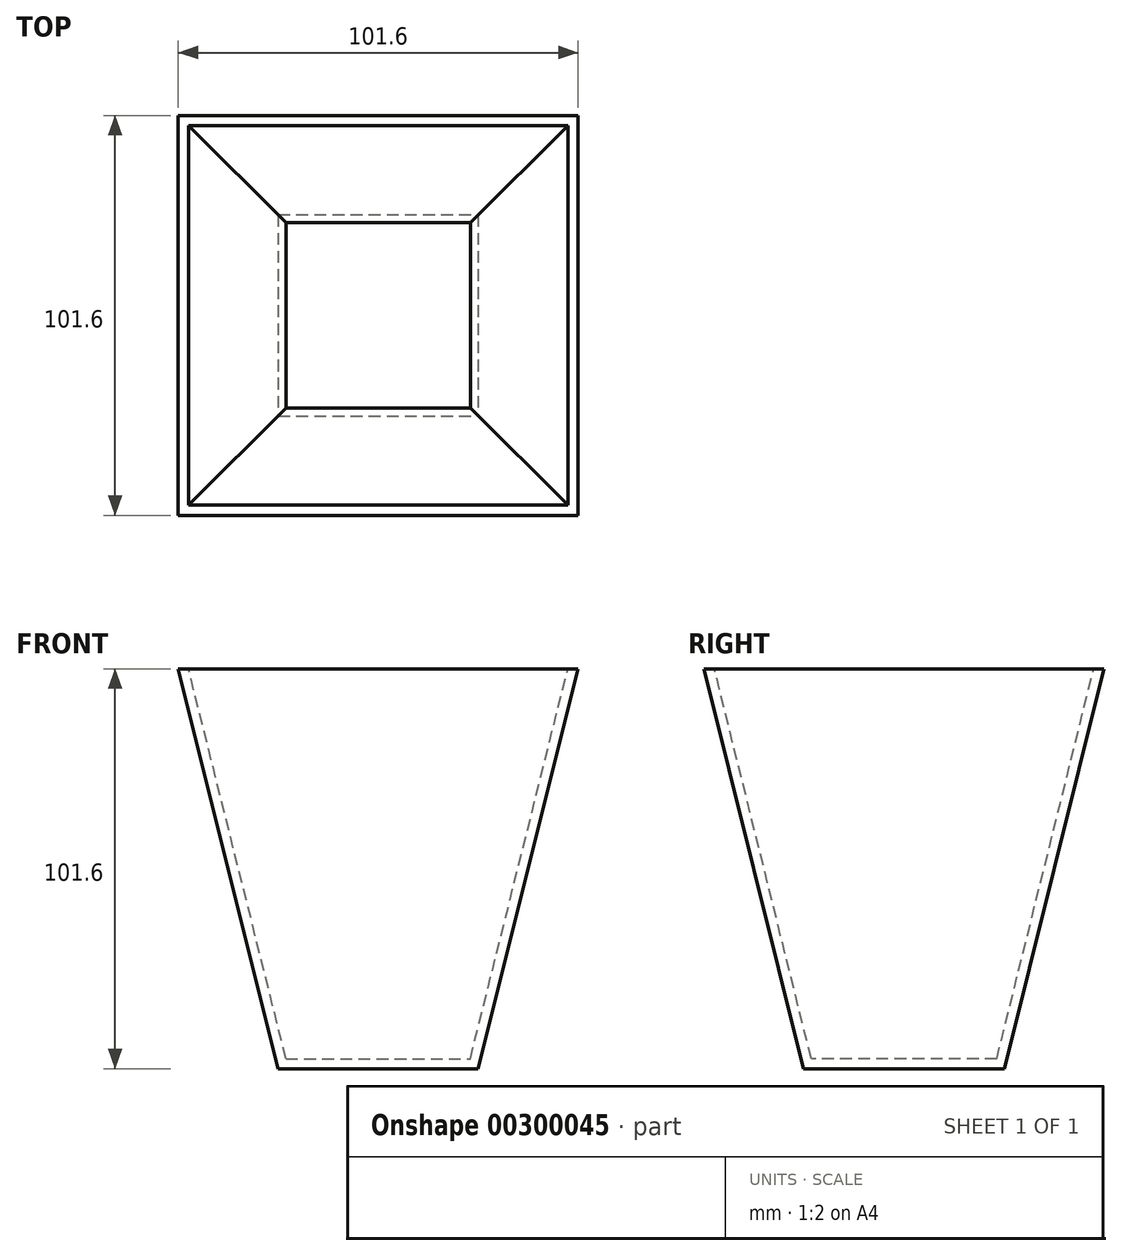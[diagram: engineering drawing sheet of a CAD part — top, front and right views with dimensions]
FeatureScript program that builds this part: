
annotation { "Feature Type Name" : "Feature", "Feature Type Description" : "" }
export const myFeature = defineFeature(function(context is Context, id is Id, definition is map)
    precondition{}
    {
        {
            var Q0;
            Q0=qCreatedBy(makeId("Front.planeOp"),FACE);
            var sketch = newSketch(context, id + "F0", { "sketchPlane" : qUnion([Q0])});
            skLineSegment(sketch, "E0.bottom", {"start": v(50.8, 50.8) * mm, "end": v(-50.8, 50.8) * mm});
            skLineSegment(sketch, "E0.top", {"start": v(50.8, -50.8) * mm, "end": v(-50.8, -50.8) * mm});
            skLineSegment(sketch, "E0.left", {"start": v(50.8, 50.8) * mm, "end": v(50.8, -50.8) * mm});
            skLineSegment(sketch, "E0.right", {"start": v(-50.8, 50.8) * mm, "end": v(-50.8, -50.8) * mm});
            skPoint(sketch, "E0.middle", {"position": v(0, 0) * mm});
            skSolve(sketch);
        }
        {
            var Q0;
            Q0 = qSketchRegion(id + "F0", true);
            extrude(context, id + "F1", {"entities" : qUnion([Q0]), "endBound" : BoundingType.SYMMETRIC, "depth" : 101.6 * mm});
        }
        {
            var Q0;
            Q0=makeQuery(id+"F1.opExtrude","CAP_FACE",FACE,{"disambiguationData":[OSD([sQuery(id+"F0.wireOp",EDGE,"E0.bottom"),sQuery(id+"F0.wireOp",EDGE,"E0.top"),sQuery(id+"F0.wireOp",EDGE,"E0.left"),sQuery(id+"F0.wireOp",EDGE,"E0.right")])],"isStart":false});
            var sketch = newSketch(context, id + "F2", { "sketchPlane" : qUnion([Q0])});
            skLineSegment(sketch, "E1", {"start": v(-50.8, 50.8) * mm, "end": v(-25.4, -50.8) * mm});
            skLineSegment(sketch, "E2", {"start": v(-25.4, -50.8) * mm, "end": v(-50.8, -50.8) * mm});
            skLineSegment(sketch, "E3", {"start": v(-50.8, -50.8) * mm, "end": v(-50.8, 50.8) * mm});
            skLineSegment(sketch, "E4.MirrorCS", {"start": v(50.8, 50.8) * mm, "end": v(25.4, -50.8) * mm});
            skLineSegment(sketch, "E5.MirrorCS", {"start": v(50.8, -50.8) * mm, "end": v(50.8, 50.8) * mm});
            skLineSegment(sketch, "E6.MirrorCS", {"start": v(25.4, -50.8) * mm, "end": v(50.8, -50.8) * mm});
            skSolve(sketch);
        }
        {
            var Q0;
            Q0 = qSketchRegion(id + "F2", true);
            extrude(context, id + "F3", {"entities" : qUnion([Q0]), "operationType" : NewBodyOperationType.REMOVE, "endBound" : BoundingType.THROUGH_ALL, "oppositeDirection" : true, "depth" : 25.4 * mm});
        }
        {
            var Q0;
            Q0=qCreatedBy(makeId("Right.planeOp"),FACE);
            cPlane(context, id + "F4", {"entities" : qUnion([Q0]), "cplaneType" : CPlaneType.OFFSET, "offset" : 50.8 * mm, "width" : 152.4 * mm, "height" : 152.4 * mm});
        }
        {
            var Q0;
            Q0=qCreatedBy(id+"F4.planeOp",FACE);
            var sketch = newSketch(context, id + "F5", { "sketchPlane" : qUnion([Q0])});
            skLineSegment(sketch, "E7", {"start": v(-50.8, 50.8) * mm, "end": v(-25.56, -50.8) * mm});
            skLineSegment(sketch, "E8", {"start": v(-25.56, -50.8) * mm, "end": v(-50.96, -50.8) * mm});
            skLineSegment(sketch, "E9", {"start": v(-50.96, -50.8) * mm, "end": v(-50.8, 50.8) * mm});
            skLineSegment(sketch, "E10.MirrorCS", {"start": v(50.8, 50.8) * mm, "end": v(25.56, -50.8) * mm});
            skLineSegment(sketch, "E11.MirrorCS", {"start": v(50.96, -50.8) * mm, "end": v(50.8, 50.8) * mm});
            skLineSegment(sketch, "E12.MirrorCS", {"start": v(25.56, -50.8) * mm, "end": v(50.96, -50.8) * mm});
            skSolve(sketch);
        }
        {
            var Q0;
            Q0 = qSketchRegion(id + "F5", true);
            extrude(context, id + "F6", {"entities" : qUnion([Q0]), "operationType" : NewBodyOperationType.REMOVE, "endBound" : BoundingType.THROUGH_ALL, "oppositeDirection" : true, "depth" : 25.4 * mm});
        }
        {
            var Q0;
            Q0=makeQuery(id+"F1.opExtrude","SWEPT_FACE",FACE,{"disambiguationData":[OSD([sQuery(id+"F0.wireOp",EDGE,"E0.bottom")])]});
            shell(context, id + "F7", {"entities" : qUnion([Q0]), "thickness" : 2.54 * mm});
        }
    });
